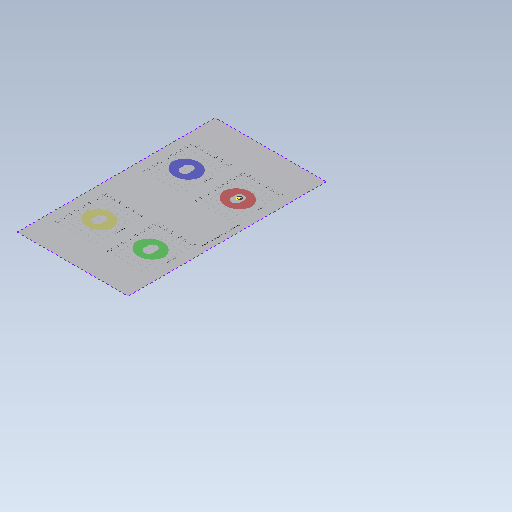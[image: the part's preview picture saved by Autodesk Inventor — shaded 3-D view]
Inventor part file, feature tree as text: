
AUTODESK INVENTOR PART (.ipt)
format: ipt  version: 2024.2 (Build 282272000, 272)  size: 172,544 bytes
history: native  units: in
note: dims shown in document units (in); Inventor stores cm internally (conversion verified against a paired STEP export)
features: other x5, sketch x1
ambient origin geometry x8: Origin, YZ Plane, XZ Plane, XY Plane, X Axis, Y Axis, Z Axis, Center Point
bodies: Body1 (feature_tree)
feature tree (6):
  other  "5 Barras Version 0.ipt"
  sketch  "Sketch1"  dims[d0=0.3937in d5=169.0728in]
  other  "Motor 2 Stator::5 Barras Version 0.ipt"
  other  "TaggingFeature1"
  other  "Image1"
  other  "Motor 2 Stator"
